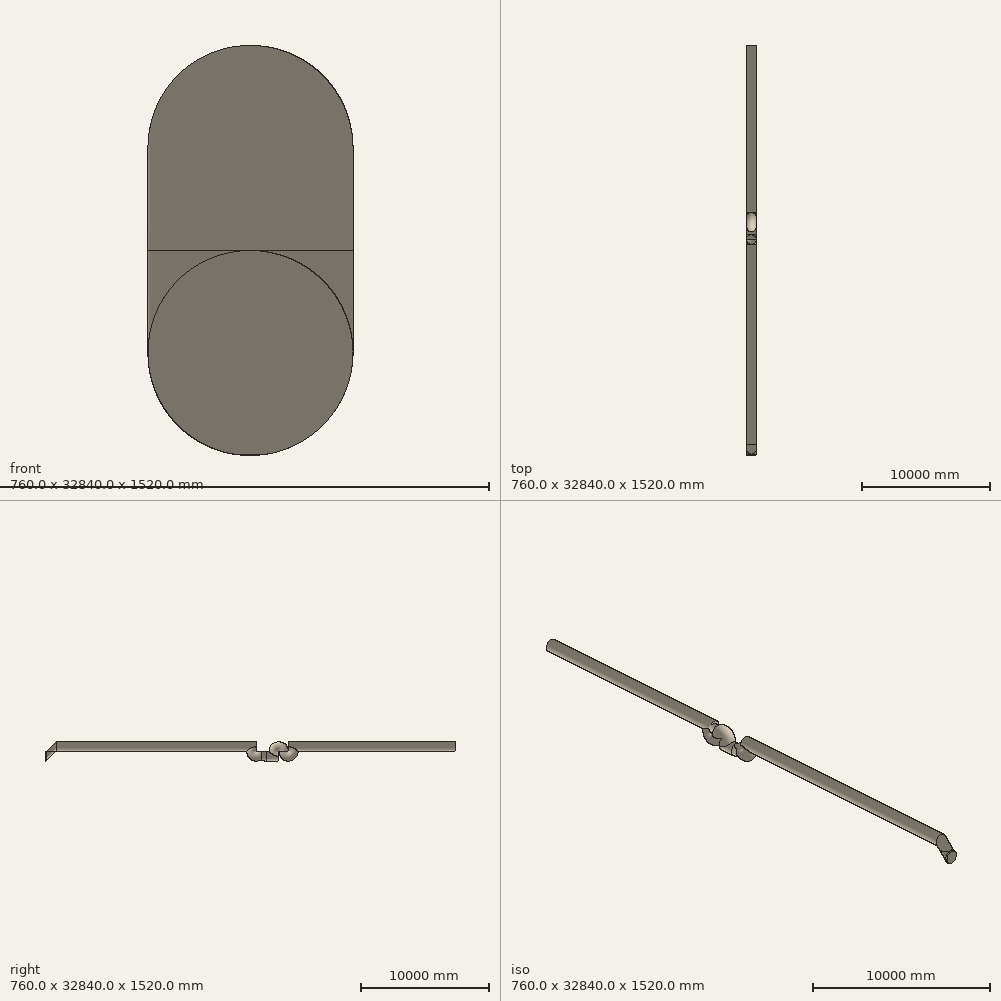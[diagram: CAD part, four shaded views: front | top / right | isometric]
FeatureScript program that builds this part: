
annotation { "Feature Type Name" : "Feature", "Feature Type Description" : "" }
export const myFeature = defineFeature(function(context is Context, id is Id, definition is map)
    precondition{}
    {
        {
            var Q0;
            Q0=qCreatedBy(makeId("Front.planeOp"),FACE);
            var sketch = newSketch(context, id + "F0", { "sketchPlane" : qUnion([Q0])});
            skCircle(sketch, "E0", {"center": v(0, 0) * mm, "radius": 380 * mm});
            skPoint(sketch, "E1", {"position": v(0, 380) * mm});
            skSolve(sketch);
        }
        {
            var Q0;
            Q0 = qSketchRegion(id + "F0", true);
            extrude(context, id + "F1", {"entities" : qUnion([Q0]), "depth" : 100 * mm});
        }
        {
            var Q0;
            Q0=qCreatedBy(makeId("Right.planeOp"),FACE);
            var sketch = newSketch(context, id + "F2", { "sketchPlane" : qUnion([Q0])});
            skArc(sketch, "E2", {"start": v(0, 0) * mm, "mid": v(268.7, 111.3) * mm, "end": v(380, 380) * mm});
            skLineSegment(sketch, "E3", {"start": v(0, 380) * mm, "end": v(760, 380) * mm, "construction": true});
            skArc(sketch, "E4", {"start": v(380, 380) * mm, "mid": v(491.3, 648.7) * mm, "end": v(760, 760) * mm});
            skSolve(sketch);
        }
        {
            var Q0;
            Q0 = qSketchRegion(id + "F0", true);
            var Q1;
            Q1=sQuery(id+"F2.wireOp",EDGE,"E2");
            var Q2;
            Q2=sQuery(id+"F2.wireOp",EDGE,"E4");
            sweep(context, id + "F3", {"operationType" : NewBodyOperationType.ADD, "profiles" : qUnion([Q0]), "path" : qUnion([Q1, Q2])});
        }
        {
            var Q0;
            Q0=makeQuery(id+"F3.opSweep","CAP_FACE",FACE,{"disambiguationData":[OSD([sQuery(id+"F0.wireOp",EDGE,"E0"),sQuery(id+"F2.wireOp",VERTEX,"E4.end")])],"isStart":false});
            var sketch = newSketch(context, id + "F4", { "sketchPlane" : qUnion([Q0])});
            skCircle(sketch, "E5", {"center": v(0, 760) * mm, "radius": 380 * mm});
            skSolve(sketch);
        }
        {
            var Q0;
            Q0=makeQuery(id+"F4.imprint","IMPRINT",FACE,{"disambiguationData":[TD([[makeQuery(id+"F4.imprint","IMPRINT",EDGE,{"derivedFrom":sQuery(id+"F4.wireOp",EDGE,"E5")}),1.0]])]});
            extrude(context, id + "F5", {"entities" : qUnion([Q0]), "operationType" : NewBodyOperationType.ADD, "depth" : 15700 * mm});
        }
        {
            var Q0;
            Q0=makeQuery(id+"F1.opExtrude","CAP_FACE",FACE,{"disambiguationData":[OSD([sQuery(id+"F0.wireOp",EDGE,"E0")])],"isStart":false});
            var sketch = newSketch(context, id + "F6", { "sketchPlane" : qUnion([Q0])});
            skLineSegment(sketch, "E6.bottom", {"start": v(-378.38, 35) * mm, "end": v(-389.1, 35) * mm});
            skLineSegment(sketch, "E6.top", {"start": v(-378.38, -35) * mm, "end": v(-389.1, -35) * mm});
            skLineSegment(sketch, "E6.left", {"start": v(-378.38, 35) * mm, "end": v(-378.38, -35) * mm});
            skLineSegment(sketch, "E6.right", {"start": v(-389.1, 35) * mm, "end": v(-389.1, -35) * mm});
            skLineSegment(sketch, "E7.bottom", {"start": v(-51.05, -376.56) * mm, "end": v(51.05, -376.56) * mm});
            skLineSegment(sketch, "E7.top", {"start": v(-51.05, -420.46) * mm, "end": v(51.05, -420.46) * mm});
            skLineSegment(sketch, "E7.left", {"start": v(-51.05, -376.56) * mm, "end": v(-51.05, -420.46) * mm});
            skLineSegment(sketch, "E7.right", {"start": v(51.05, -376.56) * mm, "end": v(51.05, -420.46) * mm});
            skSolve(sketch);
        }
        {
            var Q0;
            {var subQ0=sQuery(id+"F6.wireOp",EDGE,"E6.left");Q0=makeQuery(id+"F6.imprint","IMPRINT",FACE,{"disambiguationData":[TD([[makeQuery(id+"F6.imprint","IMPRINT",EDGE,{"derivedFrom":subQ0}),-1.0]])]});}
            var Q1;
            {var subQ0=sQuery(id+"F6.wireOp",EDGE,"E7.bottom");Q1=makeQuery(id+"F6.imprint","IMPRINT",FACE,{"disambiguationData":[TD([[makeQuery(id+"F6.imprint","IMPRINT",EDGE,{"derivedFrom":subQ0}),-1.0]])]});}
            extrude(context, id + "F7", {"entities" : qUnion([Q0, Q1]), "operationType" : NewBodyOperationType.REMOVE, "oppositeDirection" : true, "depth" : 25 * mm});
        }
        {
            var Q0;
            Q0=makeQuery(id+"F5.opExtrude","CAP_FACE",FACE,{"disambiguationData":[OSD([sQuery(id+"F4.wireOp",EDGE,"E5")])],"isStart":false});
            var sketch = newSketch(context, id + "F8", { "sketchPlane" : qUnion([Q0])});
            skCircle(sketch, "E8", {"center": v(0, 760) * mm, "radius": 380 * mm});
            skSolve(sketch);
        }
        {
            var Q0;
            Q0=qCreatedBy(makeId("Right.planeOp"),FACE);
            var sketch = newSketch(context, id + "F9", { "sketchPlane" : qUnion([Q0])});
            skArc(sketch, "E9", {"start": v(16460, 760) * mm, "mid": v(16728.7, 648.7) * mm, "end": v(16840, 380) * mm});
            skLineSegment(sketch, "E10", {"start": v(16460, 380) * mm, "end": v(18980, 380) * mm});
            skArc(sketch, "E11", {"start": v(16840, 380) * mm, "mid": v(16951.3, 111.3) * mm, "end": v(17220, 0) * mm});
            skLineSegment(sketch, "E12", {"start": v(17220, 0) * mm, "end": v(18220, 0) * mm});
            skArc(sketch, "E13", {"start": v(18220, 0) * mm, "mid": v(18488.7, 111.3) * mm, "end": v(18600, 380) * mm});
            skArc(sketch, "E14", {"start": v(18600, 380) * mm, "mid": v(18711.3, 648.7) * mm, "end": v(18980, 760) * mm});
            skLineSegment(sketch, "E15", {"start": v(18980, 760) * mm, "end": v(32080, 760) * mm});
            skSolve(sketch);
        }
        {
            var Q0;
            Q0=makeQuery(id+"F8.imprint","IMPRINT",FACE,{"disambiguationData":[TD([[makeQuery(id+"F8.imprint","IMPRINT",EDGE,{"derivedFrom":sQuery(id+"F8.wireOp",EDGE,"E8")}),1.0]])]});
            var Q1;
            Q1=sQuery(id+"F9.wireOp",EDGE,"E9");
            var Q2;
            Q2=sQuery(id+"F9.wireOp",EDGE,"E11");
            var Q3;
            Q3=sQuery(id+"F9.wireOp",EDGE,"E12");
            var Q4;
            Q4=sQuery(id+"F9.wireOp",EDGE,"E13");
            var Q5;
            Q5=sQuery(id+"F9.wireOp",EDGE,"E14");
            var Q6;
            Q6=sQuery(id+"F9.wireOp",EDGE,"E15");
            sweep(context, id + "F10", {"operationType" : NewBodyOperationType.ADD, "profiles" : qUnion([Q0]), "path" : qUnion([Q1, Q2, Q3, Q4, Q5, Q6])});
        }
    });
